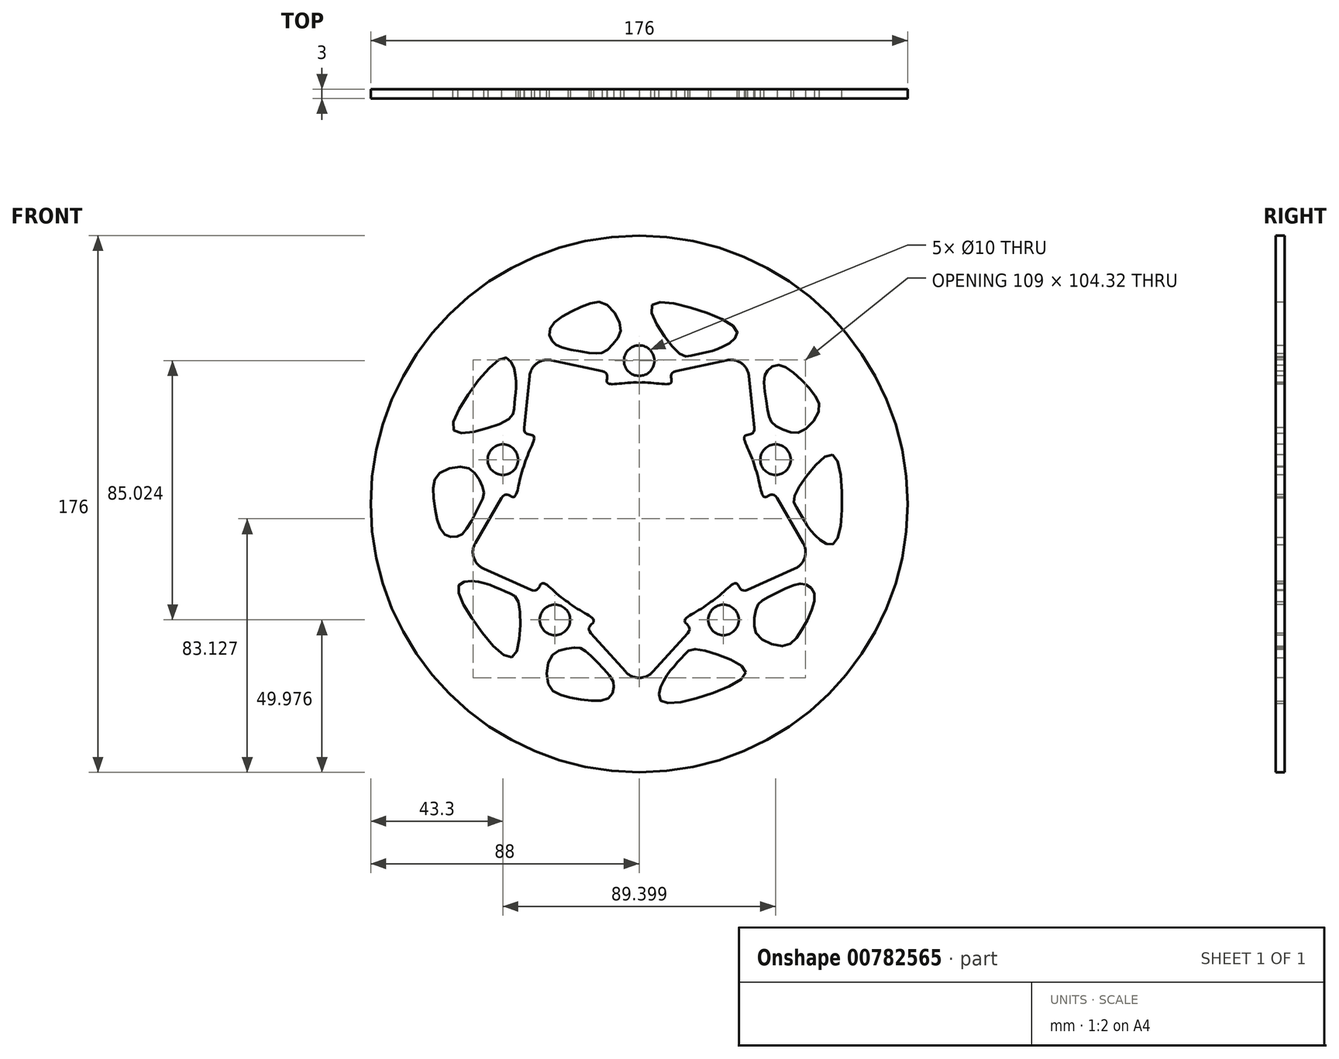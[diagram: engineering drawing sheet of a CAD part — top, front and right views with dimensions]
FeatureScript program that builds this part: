
annotation { "Feature Type Name" : "Feature", "Feature Type Description" : "" }
export const myFeature = defineFeature(function(context is Context, id is Id, definition is map)
    precondition{}
    {
        {
            var Q0;
            Q0=qCreatedBy(makeId("Front.planeOp"),FACE);
            var sketch = newSketch(context, id + "F0", { "sketchPlane" : qUnion([Q0])});
            skArc(sketch, "E0", {"start": v(51.73, 71.2) * mm, "mid": v(0, 88) * mm, "end": v(-51.73, 71.2) * mm});
            skLineSegment(sketch, "E1", {"start": v(0, 0) * mm, "end": v(51.73, 71.2) * mm});
            skLineSegment(sketch, "E2", {"start": v(0, 96.18) * mm, "end": v(0, -102.41) * mm, "construction": true});
            skLineSegment(sketch, "E3", {"start": v(-115.84, 0) * mm, "end": v(114.44, 0) * mm, "construction": true});
            skLineSegment(sketch, "E4.MirrorCS", {"start": v(0, 0) * mm, "end": v(-51.73, 71.2) * mm});
            skSolve(sketch);
        }
        {
            var Q0;
            Q0=makeQuery(id+"F0.imprint","IMPRINT",FACE,{"disambiguationData":[TD([[makeQuery(id+"F0.imprint","IMPRINT",EDGE,{"derivedFrom":sQuery(id+"F0.wireOp",EDGE,"E0")}),1.0]])]});
            extrude(context, id + "F1", {"entities" : qUnion([Q0]), "depth" : 3 * mm, "offsetDistance" : 25 * mm});
        }
        {
            var Q0;
            Q0=makeQuery(id+"F1.opExtrude","CAP_FACE",FACE,{"disambiguationData":[OSD([sQuery(id+"F0.wireOp",EDGE,"E0"),sQuery(id+"F0.wireOp",EDGE,"E1"),sQuery(id+"F0.wireOp",EDGE,"E4.MirrorCS")])],"isStart":false});
            var sketch = newSketch(context, id + "F2", { "sketchPlane" : qUnion([Q0])});
            skLineSegment(sketch, "E5", {"start": v(0, 0) * mm, "end": v(35.27, 48.54) * mm, "construction": true});
            skPoint(sketch, "E6.visualSharp", {"position": v(35.27, 48.54) * mm});
            skArc(sketch, "E7", {"start": v(0, 52) * mm, "mid": v(5, 47) * mm, "end": v(0, 42) * mm});
            skLineSegment(sketch, "E8", {"start": v(28.75, 47.16) * mm, "end": v(12.12, 43.62) * mm});
            skArc(sketch, "E9.filletArc", {"start": v(35.96, 41.91) * mm, "mid": v(33.52, 46.14) * mm, "end": v(28.75, 47.16) * mm});
            skFitSpline(sketch, "E10", {"points": [v(0, 39.8) * mm, v(10.55, 39.9) * mm, v(12.12, 43.62) * mm], "startDerivative": vector(20.69, 1.94) * mm, "endDerivative": vector(20.96, 4.97) * mm});
            skArc(sketch, "E11.MirrorCS", {"start": v(0, 52) * mm, "mid": v(-5, 47) * mm, "end": v(0, 42) * mm});
            skFitSpline(sketch, "E12.MirrorCS", {"points": [v(0, 39.8) * mm, v(-10.55, 39.9) * mm, v(-12.12, 43.62) * mm], "startDerivative": vector(-20.69, 1.94) * mm, "endDerivative": vector(-20.96, 4.97) * mm});
            skLineSegment(sketch, "E13.MirrorCS", {"start": v(-28.75, 47.16) * mm, "end": v(-12.12, 43.62) * mm});
            skArc(sketch, "E14.MirrorCS", {"start": v(-35.96, 41.91) * mm, "mid": v(-33.52, 46.14) * mm, "end": v(-28.75, 47.16) * mm});
            skLineSegment(sketch, "E15", {"start": v(-35.96, 41.91) * mm, "end": v(-2.94, -4.94) * mm});
            skLineSegment(sketch, "E16", {"start": v(-2.94, -4.94) * mm, "end": v(12.78, -4.94) * mm});
            skLineSegment(sketch, "E17", {"start": v(12.78, -4.94) * mm, "end": v(35.96, 41.91) * mm});
            skFitSpline(sketch, "E18", {"points": [v(-28.6, 53.5) * mm, v(-26.4, 51.67) * mm, v(-19.48, 50.1) * mm, v(-14.14, 49.36) * mm, v(-11.35, 49.97) * mm, v(-7.7, 53.5) * mm, v(-6.12, 58.1) * mm, v(-11.1, 65.64) * mm, v(-17.18, 65.4) * mm, v(-25.92, 61.02) * mm, v(-29.44, 56.88) * mm, v(-28.6, 53.5) * mm]});
            skFitSpline(sketch, "E19", {"points": [v(4.22, 65.26) * mm, v(7.78, 55.7) * mm, v(14.43, 48.56) * mm, v(17.03, 48.67) * mm, v(19.42, 49.2) * mm, v(21.7, 49.72) * mm, v(24.16, 50.29) * mm, v(27.08, 51.42) * mm, v(30.57, 53.49) * mm, v(32.1, 56.67) * mm, v(19.3, 63.64) * mm, v(4.22, 65.26) * mm]});
            skSolve(sketch);
        }
        {
            var Q0;
            Q0 = qSketchRegion(id + "F2", true);
            var Q1;
            Q1 = qSketchRegion(id + "F4SIeHR8vNL3SW5_1", true);
            extrude(context, id + "F3", {"entities" : qUnion([Q0, Q1]), "operationType" : NewBodyOperationType.REMOVE, "endBound" : BoundingType.THROUGH_ALL, "oppositeDirection" : true, "depth" : 25 * mm, "offsetDistance" : 25 * mm});
        }
        {
            var Q0;
            Q0=qCreatedBy(makeId("Right.planeOp"),FACE);
            var sketch = newSketch(context, id + "F4", { "sketchPlane" : qUnion([Q0])});
            skLineSegment(sketch, "E20", {"start": v(0, 0) * mm, "end": v(-77.77, 0) * mm, "construction": true});
            skSolve(sketch);
        }
        {
            var Q0;
            Q0=makeQuery(id+"F1.opExtrude","SWEPT_BODY",BODY,{"disambiguationData":[OSD([sQuery(id+"F0.wireOp",EDGE,"E0"),sQuery(id+"F0.wireOp",EDGE,"E1"),sQuery(id+"F0.wireOp",EDGE,"E4.MirrorCS")])]});
            var Q1;
            Q1=sQuery(id+"F4.wireOp",EDGE,"E20");
            circularPattern(context, id + "F5", {"operationType" : NewBodyOperationType.ADD, "entities" : qUnion([Q0]), "axis" : qUnion([Q1]), "angle" : 360 * degree, "instanceCount" : 5, "equalSpace" : true});
        }
    });
